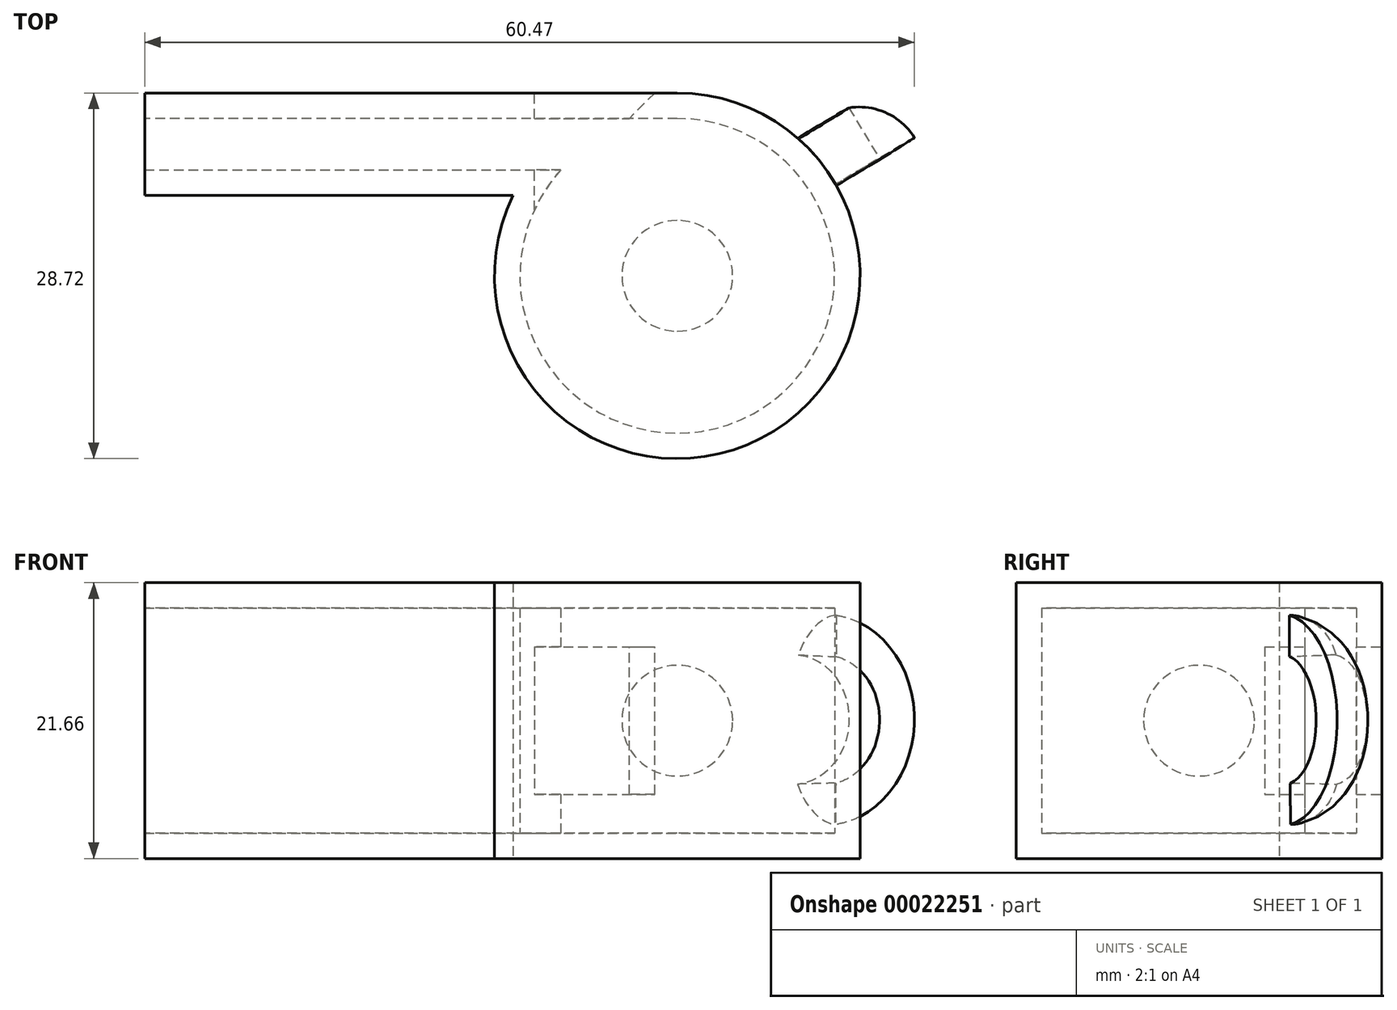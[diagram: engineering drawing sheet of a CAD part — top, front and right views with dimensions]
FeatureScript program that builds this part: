
annotation { "Feature Type Name" : "Feature", "Feature Type Description" : "" }
export const myFeature = defineFeature(function(context is Context, id is Id, definition is map)
    precondition{}
    {
        {
            var Q0;
            Q0=qCreatedBy(makeId("Top.planeOp"),FACE);
            var sketch = newSketch(context, id + "F0", { "sketchPlane" : qUnion([Q0]), "disableImprinting" : false});
            skArc(sketch, "E0", {"start": v(-12.9, 6.31) * mm, "mid": v(7.6, -12.19) * mm, "end": v(0, 14.36) * mm});
            skLineSegment(sketch, "E1", {"start": v(0, 14.36) * mm, "end": v(-41.84, 14.36) * mm});
            skLineSegment(sketch, "E2", {"start": v(-41.84, 14.36) * mm, "end": v(-41.84, 6.31) * mm});
            skLineSegment(sketch, "E3", {"start": v(-41.84, 6.31) * mm, "end": v(-12.9, 6.31) * mm});
            skSolve(sketch);
        }
        {
            var Q0;
            Q0=makeQuery(id+"F0.imprint","IMPRINT",FACE,{"disambiguationData":[TD([[makeQuery(id+"F0.imprint","IMPRINT",EDGE,{"derivedFrom":sQuery(id+"F0.wireOp",EDGE,"E0")}),1.0]])]});
            extrude(context, id + "F1", {"entities" : qUnion([Q0]), "flatOperationType" : FlatOperationType.REMOVE, "thickness1" : 6.35 * mm, "thickness2" : 0 * mm, "offsetDistance" : 25.4 * mm, "startOffsetBound" : StartOffsetType.BLIND, "startOffsetDistance" : 25.4 * mm, "depth" : 21.67 * mm, "symmetric" : true, "domain" : OperationDomain.MODEL});
        }
        {
            var Q0;
            Q0=makeQuery(id+"F1.opExtrude","SWEPT_FACE",FACE,{"disambiguationData":[OSD([sQuery(id+"F0.wireOp",EDGE,"E2")])]});
            shell(context, id + "F2", {"entities" : qUnion([Q0]), "thickness" : 2 * mm});
        }
        {
            var Q0;
            Q0=qCreatedBy(makeId("Top.planeOp"),FACE);
            var sketch = newSketch(context, id + "F3", { "sketchPlane" : qUnion([Q0]), "disableImprinting" : false});
            skArc(sketch, "E4", {"start": v(0, 4.35) * mm, "mid": v(-4.35, 0) * mm, "end": v(0, -4.35) * mm});
            skLineSegment(sketch, "E5", {"start": v(0, 4.35) * mm, "end": v(0, -4.35) * mm});
            skLineSegment(sketch, "E6", {"start": v(0, 9.47) * mm, "end": v(0, -10.41) * mm, "construction": true});
            skSolve(sketch);
        }
        {
            var Q0;
            Q0=makeQuery(id+"F3.imprint","IMPRINT",FACE,{"disambiguationData":[TD([[makeQuery(id+"F3.imprint","IMPRINT",EDGE,{"derivedFrom":sQuery(id+"F3.wireOp",EDGE,"E4")}),1.0]])]});
            var Q1;
            Q1=sQuery(id+"F3.wireOp",EDGE,"E6");
            revolve(context, id + "F4", {"surfaceOperationType" : NewSurfaceOperationType.NEW, "entities" : qUnion([Q0]), "thickness1" : 6.35 * mm, "thickness2" : 0 * mm, "thickness" : 6.35 * mm, "axis" : qUnion([Q1]), "revolveType" : RevolveType.FULL});
        }
        {
            var Q0;
            Q0=makeQuery(id+"F1.opExtrude","CAP_VERTEX",VERTEX,{"disambiguationData":[OSD([sQuery(id+"F0.wireOp",EDGE,"E1"),sQuery(id+"F0.wireOp",EDGE,"E2")])],"isStart":true});
            var Q1;
            Q1=makeQuery(id+"F1.opExtrude","CAP_VERTEX",VERTEX,{"disambiguationData":[OSD([sQuery(id+"F0.wireOp",EDGE,"E1"),sQuery(id+"F0.wireOp",EDGE,"E2")])],"isStart":false});
            var Q2;
            Q2=makeQuery(id+"F1.opExtrude","CAP_VERTEX",VERTEX,{"disambiguationData":[OSD([sQuery(id+"F0.wireOp",EDGE,"E0"),sQuery(id+"F0.wireOp",EDGE,"E1")])],"isStart":false});
            cPlane(context, id + "F5", {"entities" : qUnion([Q0, Q1, Q2]), "cplaneType" : CPlaneType.THREE_POINT, "offset" : 152.4 * mm, "width" : 152.4 * mm, "height" : 152.4 * mm});
        }
        {
            var Q0;
            Q0=qCreatedBy(id+"F5.planeOp",FACE);
            var sketch = newSketch(context, id + "F6", { "sketchPlane" : qUnion([Q0]), "disableImprinting" : false});
            skLineSegment(sketch, "E7.rect.bottom", {"start": v(-4.77, 5.79) * mm, "end": v(-11.23, 5.79) * mm});
            skLineSegment(sketch, "E7.rect.top", {"start": v(-4.77, -5.79) * mm, "end": v(-11.23, -5.79) * mm});
            skLineSegment(sketch, "E7.rect.left", {"start": v(-4.77, 5.79) * mm, "end": v(-4.77, -5.79) * mm});
            skLineSegment(sketch, "E7.rect.right", {"start": v(-11.23, 5.79) * mm, "end": v(-11.23, -5.79) * mm});
            skPoint(sketch, "E7.rect.middle", {"position": v(-8, 0) * mm});
            skSolve(sketch);
        }
        {
            var Q0;
            Q0=makeQuery(id+"F6.imprint","IMPRINT",FACE,{"disambiguationData":[TD([[makeQuery(id+"F6.imprint","IMPRINT",EDGE,{"derivedFrom":sQuery(id+"F6.wireOp",EDGE,"E7.rect.bottom")}),1.0]])]});
            extrude(context, id + "F7", {"entities" : qUnion([Q0]), "operationType" : NewBodyOperationType.REMOVE, "flatOperationType" : FlatOperationType.REMOVE, "thickness1" : 6.35 * mm, "thickness2" : 0 * mm, "offsetDistance" : 25.4 * mm, "startOffsetBound" : StartOffsetType.BLIND, "startOffsetDistance" : 25.4 * mm, "depth" : 36.27 * mm, "symmetric" : true, "domain" : OperationDomain.MODEL});
        }
        {
            var Q0;
            Q0=makeQuery(id+"F7.boolean.opBoolean","INTERSECT",EDGE,{"derivedFrom":[makeQuery(id+"F1.opExtrude","SWEPT_FACE",FACE,{"disambiguationData":[OSD([sQuery(id+"F0.wireOp",EDGE,"E1")])]}),makeQuery(id+"F7.opExtrude","SWEPT_FACE",FACE,{"disambiguationData":[OSD([sQuery(id+"F6.wireOp",EDGE,"E7.rect.left")])]})]});
            chamfer(context, id + "F8", {"entities" : qUnion([Q0]), "width" : 3 * mm});
        }
        {
            var Q0;
            Q0=makeQuery(id+"F1.opExtrude","CAP_FACE",FACE,{"disambiguationData":[OSD([sQuery(id+"F0.wireOp",EDGE,"E0"),sQuery(id+"F0.wireOp",EDGE,"E1"),sQuery(id+"F0.wireOp",EDGE,"E2"),sQuery(id+"F0.wireOp",EDGE,"E3")])],"isStart":false});
            var sketch = newSketch(context, id + "F9", { "sketchPlane" : qUnion([Q0]), "disableImprinting" : false});
            skLineSegment(sketch, "E8", {"start": v(11.04, 9.18) * mm, "end": v(33.93, 22.71) * mm, "construction": true});
            skSolve(sketch);
        }
        {
            var Q0;
            Q0=makeQuery(id+"F1.opExtrude","CAP_FACE",FACE,{"disambiguationData":[OSD([sQuery(id+"F0.wireOp",EDGE,"E0"),sQuery(id+"F0.wireOp",EDGE,"E1"),sQuery(id+"F0.wireOp",EDGE,"E2"),sQuery(id+"F0.wireOp",EDGE,"E3")])],"isStart":true});
            var sketch = newSketch(context, id + "F10", { "sketchPlane" : qUnion([Q0]), "disableImprinting" : false});
            skLineSegment(sketch, "E9", {"start": v(11.1, -9.12) * mm, "end": v(33.93, -22.9) * mm, "construction": true});
            skSolve(sketch);
        }
        {
            var Q0;
            Q0=sQuery(id+"F10.wireOp",VERTEX,"E9.end");
            var Q1;
            Q1=sQuery(id+"F9.wireOp",VERTEX,"E8.end");
            var Q2;
            Q2=sQuery(id+"F10.wireOp",VERTEX,"E9.start");
            cPlane(context, id + "F11", {"entities" : qUnion([Q0, Q1, Q2]), "cplaneType" : CPlaneType.THREE_POINT, "offset" : 152.4 * mm, "width" : 152.4 * mm, "height" : 152.4 * mm});
        }
        {
            var Q0;
            Q0=qCreatedBy(id+"F11.planeOp",FACE);
            var sketch = newSketch(context, id + "F12", { "sketchPlane" : qUnion([Q0])});
            skArc(sketch, "E10", {"start": v(-13.27, 8.29) * mm, "mid": v(-21.56, 0) * mm, "end": v(-13.27, -8.29) * mm});
            skArc(sketch, "E11", {"start": v(-13.27, 5.1) * mm, "mid": v(-18.37, 0) * mm, "end": v(-13.27, -5.1) * mm});
            skLineSegment(sketch, "E12", {"start": v(-13.27, -8.29) * mm, "end": v(-13.27, -5.1) * mm});
            skLineSegment(sketch, "E13.trimOffspring", {"start": v(-13.27, 5.1) * mm, "end": v(-13.27, 8.29) * mm});
            skLineSegment(sketch, "E14", {"start": v(-13.27, 13.08) * mm, "end": v(-13.27, -14.16) * mm, "construction": true});
            skSolve(sketch);
        }
        {
            var Q0;
            Q0=makeQuery(id+"F12.imprint","IMPRINT",FACE,{"disambiguationData":[TD([[makeQuery(id+"F12.imprint","IMPRINT",EDGE,{"derivedFrom":sQuery(id+"F12.wireOp",EDGE,"E10")}),1.0]])]});
            extrude(context, id + "F13", {"entities" : qUnion([Q0]), "operationType" : NewBodyOperationType.ADD, "depth" : 4.66 * mm, "symmetric" : true});
        }
        {
            var Q0;
            Q0=makeQuery(id+"F13.opExtrude","CAP_EDGE",EDGE,{"disambiguationData":[OSD([sQuery(id+"F12.wireOp",EDGE,"E10")])],"isStart":false});
            fillet(context, id + "F14", {"entities" : qUnion([Q0]), "radius" : 5.08 * mm, "tangentPropagation" : true, "allowEdgeOverflow" : false});
        }
    });
